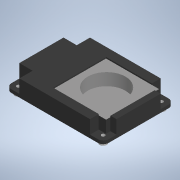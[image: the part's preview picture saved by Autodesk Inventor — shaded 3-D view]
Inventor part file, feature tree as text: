
AUTODESK INVENTOR PART (.ipt)
format: ipt  version: 2022 (Build 260153000, 153)  size: 215,552 bytes
history: native  units: mm
features: extrude x4, sketch x4, other x1, projected_geometry x1
ambient origin geometry x8: Origin, YZ Plane, XZ Plane, XY Plane, X Axis, Y Axis, Z Axis, Center Point
bodies: Body1 (feature_tree)
feature tree (10):
  other  "Твердое тело1"
  extrude  "Выдавливание1"  Depth=55.0mm
  extrude  "Выдавливание2"  Depth=40.0mm
  extrude  "Выдавливание3"  Depth=3.0mm
  extrude  "Выдавливание4"  Depth=3.0mm
  sketch  "Эскиз1"
  sketch  "Эскиз2"
  sketch  "Эскиз3"
  projected_geometry  "Спроецированная петля1"
  sketch  "Эскиз4"
